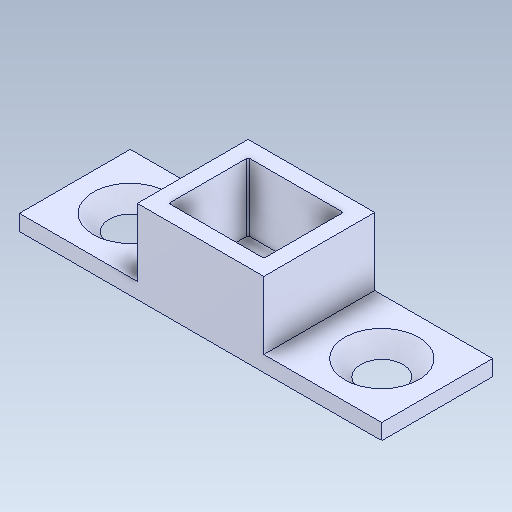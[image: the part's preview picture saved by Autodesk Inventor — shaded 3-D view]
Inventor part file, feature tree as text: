
AUTODESK INVENTOR PART (.ipt)
format: ipt  version: 2021 (Build 250183000, 183)  size: 130,048 bytes
history: mixed  units: in
note: dims shown in document units (in); Inventor stores cm internally (conversion verified against a paired STEP export)
features: mirror x1, imported_body x1
ambient origin geometry x8: Origin, YZ Plane, XZ Plane, XY Plane, X Axis, Y Axis, Z Axis, Center Point
bodies: Solid1 (imported_parasolid)
feature tree (2):
  mirror  "Mirror1"
  imported_body  NMx_Import_Brep_tag  [imported B-rep: ~26 faces, bbox_mm=[46.1, 10.6, 14.1]]
